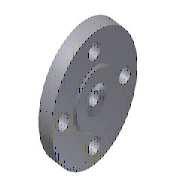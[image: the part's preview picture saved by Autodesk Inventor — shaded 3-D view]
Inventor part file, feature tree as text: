
AUTODESK INVENTOR PART (.ipt)
format: ipt  version: 2024.2 (Build 282272000, 272)  size: 217,088 bytes
history: native  units: mm
features: revolve x1, extrude x1, pattern_circular x1
ambient origin geometry x8: Origin, YZ Plane, XZ Plane, XY Plane, X Axis, Y Axis, Z Axis, Center Point
bodies: Solid1 (feature_tree)
feature tree (3):
  revolve  "Revolution1"  [1 undecoded]
  extrude  "Extrusion1"  Depth=470.0mm
  pattern_circular  "Circular Pattern1"  Angle=90.0deg  [1 undecoded]
note: 2 required parameter values undecoded (feature->parameter linkage not recoverable at this tier; creation-order binding heuristic only, values carry confidence <= 0.55)